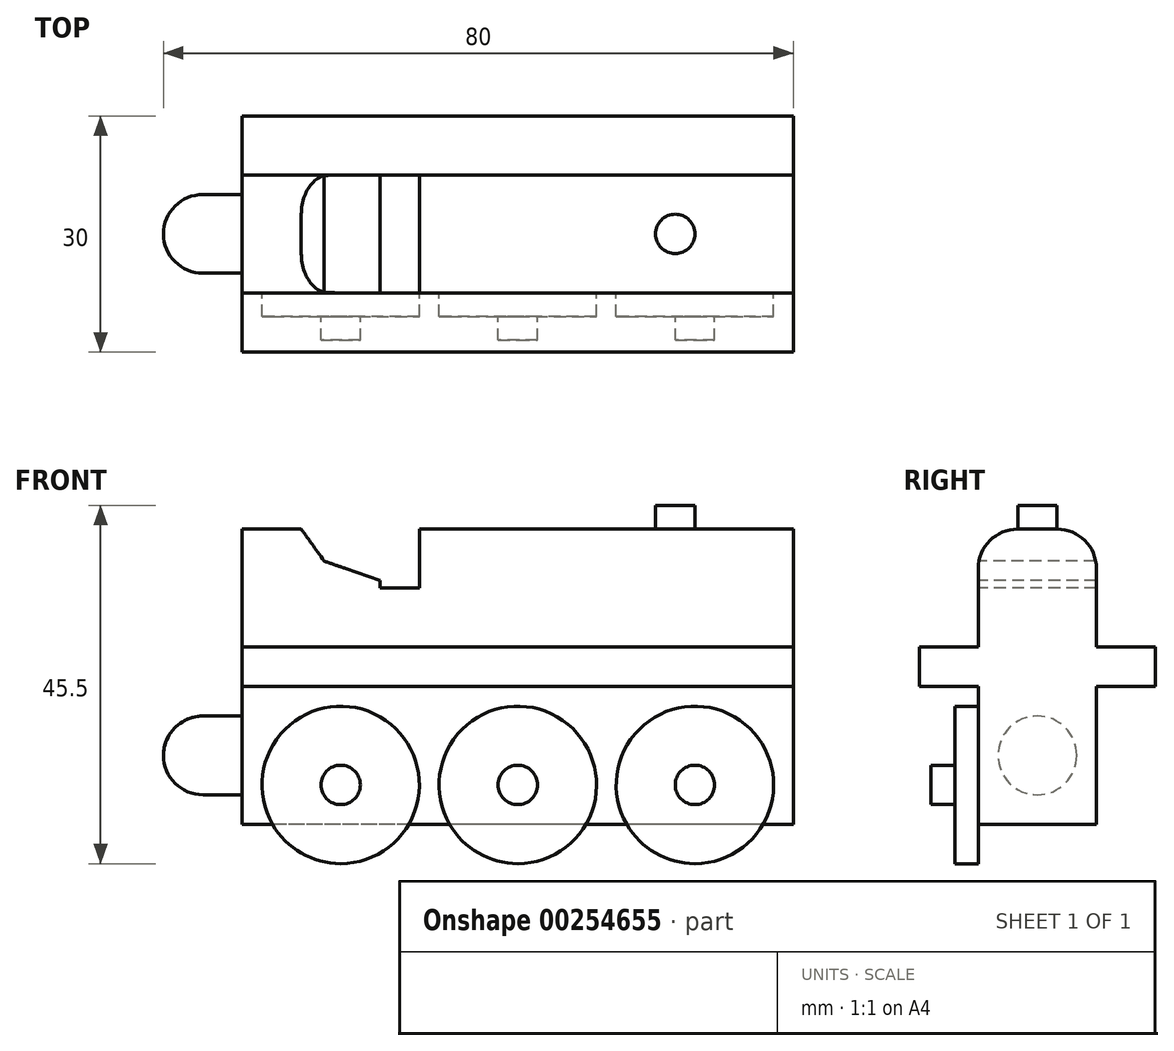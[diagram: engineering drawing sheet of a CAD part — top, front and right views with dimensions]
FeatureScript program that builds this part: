
annotation { "Feature Type Name" : "Feature", "Feature Type Description" : "" }
export const myFeature = defineFeature(function(context is Context, id is Id, definition is map)
    precondition{}
    {
        {
            var Q0;
            Q0=qCreatedBy(makeId("Top.planeOp"),FACE);
            var sketch = newSketch(context, id + "F0", { "sketchPlane" : qUnion([Q0])});
            skLineSegment(sketch, "E0.bottom", {"start": v(35, 7.5) * mm, "end": v(-35, 7.5) * mm});
            skLineSegment(sketch, "E0.top", {"start": v(35, -7.5) * mm, "end": v(-35, -7.5) * mm});
            skLineSegment(sketch, "E0.left", {"start": v(35, 7.5) * mm, "end": v(35, -7.5) * mm});
            skLineSegment(sketch, "E0.right", {"start": v(-35, 7.5) * mm, "end": v(-35, -7.5) * mm});
            skPoint(sketch, "E0.middle", {"position": v(0, 0) * mm});
            skSolve(sketch);
        }
        {
            var Q0;
            Q0 = qSketchRegion(id + "F0", true);
            extrude(context, id + "F1", {"entities" : qUnion([Q0]), "endBound" : BoundingType.SYMMETRIC, "depth" : 17.5 * mm});
        }
        {
            var Q0;
            Q0=makeQuery(id+"F1.opExtrude","CAP_FACE",FACE,{"disambiguationData":[OSD([sQuery(id+"F0.wireOp",EDGE,"E0.bottom"),sQuery(id+"F0.wireOp",EDGE,"E0.top"),sQuery(id+"F0.wireOp",EDGE,"E0.left"),sQuery(id+"F0.wireOp",EDGE,"E0.right")])],"isStart":false});
            var sketch = newSketch(context, id + "F2", { "sketchPlane" : qUnion([Q0])});
            skLineSegment(sketch, "E1.bottom", {"start": v(35, 15) * mm, "end": v(-35, 15) * mm});
            skLineSegment(sketch, "E1.top", {"start": v(35, -15) * mm, "end": v(-35, -15) * mm});
            skLineSegment(sketch, "E1.left", {"start": v(35, 15) * mm, "end": v(35, -15) * mm});
            skLineSegment(sketch, "E1.right", {"start": v(-35, 15) * mm, "end": v(-35, -15) * mm});
            skPoint(sketch, "E1.middle", {"position": v(0, 0) * mm});
            skSolve(sketch);
        }
        {
            var Q0;
            Q0 = qSketchRegion(id + "F2", true);
            extrude(context, id + "F3", {"entities" : qUnion([Q0]), "operationType" : NewBodyOperationType.ADD, "depth" : 5 * mm});
        }
        {
            var Q0;
            Q0=makeQuery(id+"F3.opExtrude","CAP_FACE",FACE,{"disambiguationData":[OSD([sQuery(id+"F2.wireOp",EDGE,"E1.bottom"),sQuery(id+"F2.wireOp",EDGE,"E1.top"),sQuery(id+"F2.wireOp",EDGE,"E1.left"),sQuery(id+"F2.wireOp",EDGE,"E1.right")])],"isStart":false});
            var sketch = newSketch(context, id + "F4", { "sketchPlane" : qUnion([Q0])});
            skLineSegment(sketch, "E2.bottom", {"start": v(35, 7.5) * mm, "end": v(-35, 7.5) * mm});
            skLineSegment(sketch, "E2.top", {"start": v(35, -7.5) * mm, "end": v(-35, -7.5) * mm});
            skLineSegment(sketch, "E2.left", {"start": v(35, 7.5) * mm, "end": v(35, -7.5) * mm});
            skLineSegment(sketch, "E2.right", {"start": v(-35, 7.5) * mm, "end": v(-35, -7.5) * mm});
            skPoint(sketch, "E2.middle", {"position": v(0, 0) * mm});
            skSolve(sketch);
        }
        {
            var Q0;
            Q0 = qSketchRegion(id + "F4", true);
            extrude(context, id + "F5", {"entities" : qUnion([Q0]), "operationType" : NewBodyOperationType.ADD, "depth" : 15 * mm});
        }
        {
            var Q0;
            Q0=qCreatedBy(makeId("Front.planeOp"),FACE);
            var sketch = newSketch(context, id + "F6", { "sketchPlane" : qUnion([Q0])});
            skLineSegment(sketch, "E3", {"start": v(-42.6, 0) * mm, "end": v(43.32, 0) * mm, "construction": true});
            skLineSegment(sketch, "E4.bottom", {"start": v(-35, 0) * mm, "end": v(-40, 0) * mm});
            skLineSegment(sketch, "E4.top", {"start": v(-35, -5) * mm, "end": v(-40, -5) * mm});
            skLineSegment(sketch, "E4.left", {"start": v(-35, 0) * mm, "end": v(-35, -5) * mm});
            skLineSegment(sketch, "E4.right", {"start": v(-40, 0) * mm, "end": v(-40, -5) * mm});
            skSolve(sketch);
        }
        {
            var Q0;
            Q0 = qSketchRegion(id + "F6", true);
            var Q1;
            Q1=sQuery(id+"F6.wireOp",EDGE,"E3");
            revolve(context, id + "F7", {"operationType" : NewBodyOperationType.ADD, "entities" : qUnion([Q0]), "axis" : qUnion([Q1]), "revolveType" : RevolveType.FULL});
        }
        {
            var Q0;
            Q0=makeQuery(id+"F1.opExtrude","SWEPT_FACE",FACE,{"disambiguationData":[OSD([sQuery(id+"F0.wireOp",EDGE,"E0.top")])]});
            var sketch = newSketch(context, id + "F8", { "sketchPlane" : qUnion([Q0])});
            skCircle(sketch, "E5", {"center": v(-22.5, -3.75) * mm, "radius": 10 * mm});
            skSolve(sketch);
        }
        {
            var Q0;
            Q0 = qSketchRegion(id + "F8", true);
            extrude(context, id + "F9", {"entities" : qUnion([Q0]), "operationType" : NewBodyOperationType.ADD, "depth" : 3 * mm});
        }
        {
            var Q0;
            Q0=makeQuery(id+"F1.opExtrude","SWEPT_FACE",FACE,{"disambiguationData":[OSD([sQuery(id+"F0.wireOp",EDGE,"E0.top")])]});
            var sketch = newSketch(context, id + "F10", { "sketchPlane" : qUnion([Q0])});
            skCircle(sketch, "E6", {"center": v(0, -3.75) * mm, "radius": 10 * mm});
            skSolve(sketch);
        }
        {
            var Q0;
            Q0 = qSketchRegion(id + "F10", true);
            extrude(context, id + "F11", {"entities" : qUnion([Q0]), "operationType" : NewBodyOperationType.ADD, "depth" : 3 * mm});
        }
        {
            var Q0;
            Q0=makeQuery(id+"F1.opExtrude","SWEPT_FACE",FACE,{"disambiguationData":[OSD([sQuery(id+"F0.wireOp",EDGE,"E0.top")])]});
            var sketch = newSketch(context, id + "F12", { "sketchPlane" : qUnion([Q0])});
            skCircle(sketch, "E7", {"center": v(22.5, -3.75) * mm, "radius": 10 * mm});
            skSolve(sketch);
        }
        {
            var Q0;
            Q0 = qSketchRegion(id + "F12", true);
            extrude(context, id + "F13", {"entities" : qUnion([Q0]), "operationType" : NewBodyOperationType.ADD, "depth" : 3 * mm});
        }
        {
            var Q0;
            Q0=makeQuery(id+"F9.opExtrude","CAP_FACE",FACE,{"disambiguationData":[OSD([sQuery(id+"F8.wireOp",EDGE,"E5")])],"isStart":false});
            var sketch = newSketch(context, id + "F14", { "sketchPlane" : qUnion([Q0])});
            skCircle(sketch, "E8", {"center": v(-22.5, -3.75) * mm, "radius": 2.5 * mm});
            skSolve(sketch);
        }
        {
            var Q0;
            Q0=makeQuery(id+"F14.imprint","IMPRINT",FACE,{"disambiguationData":[TD([[makeQuery(id+"F14.imprint","IMPRINT",EDGE,{"derivedFrom":sQuery(id+"F14.wireOp",EDGE,"E8")}),1.0]])]});
            extrude(context, id + "F15", {"entities" : qUnion([Q0]), "operationType" : NewBodyOperationType.ADD, "depth" : 3 * mm});
        }
        {
            var Q0;
            Q0=makeQuery(id+"F11.opExtrude","CAP_FACE",FACE,{"disambiguationData":[OSD([sQuery(id+"F10.wireOp",EDGE,"E6")])],"isStart":false});
            var sketch = newSketch(context, id + "F16", { "sketchPlane" : qUnion([Q0])});
            skCircle(sketch, "E9", {"center": v(0, -3.75) * mm, "radius": 2.5 * mm});
            skSolve(sketch);
        }
        {
            var Q0;
            Q0 = qSketchRegion(id + "F16", true);
            extrude(context, id + "F17", {"entities" : qUnion([Q0]), "operationType" : NewBodyOperationType.ADD, "depth" : 3 * mm});
        }
        {
            var Q0;
            Q0=makeQuery(id+"F13.opExtrude","CAP_FACE",FACE,{"disambiguationData":[OSD([sQuery(id+"F12.wireOp",EDGE,"E7")])],"isStart":false});
            var sketch = newSketch(context, id + "F18", { "sketchPlane" : qUnion([Q0])});
            skCircle(sketch, "E10", {"center": v(22.5, -3.75) * mm, "radius": 2.5 * mm});
            skSolve(sketch);
        }
        {
            var Q0;
            Q0 = qSketchRegion(id + "F18", true);
            extrude(context, id + "F19", {"entities" : qUnion([Q0]), "operationType" : NewBodyOperationType.ADD, "depth" : 3 * mm});
        }
        {
            var Q0;
            Q0=makeQuery(id+"F5.opExtrude","CAP_FACE",FACE,{"disambiguationData":[OSD([sQuery(id+"F4.wireOp",EDGE,"E2.bottom"),sQuery(id+"F4.wireOp",EDGE,"E2.top"),sQuery(id+"F4.wireOp",EDGE,"E2.left"),sQuery(id+"F4.wireOp",EDGE,"E2.right")])],"isStart":false});
            var sketch = newSketch(context, id + "F20", { "sketchPlane" : qUnion([Q0])});
            skCircle(sketch, "E11", {"center": v(20, 0) * mm, "radius": 2.5 * mm});
            skSolve(sketch);
        }
        {
            var Q0;
            Q0 = qSketchRegion(id + "F20", true);
            extrude(context, id + "F21", {"entities" : qUnion([Q0]), "operationType" : NewBodyOperationType.ADD, "depth" : 3 * mm});
        }
        {
            var Q0;
            Q0=makeQuery(id+"F5.opExtrude","SWEPT_FACE",FACE,{"disambiguationData":[OSD([sQuery(id+"F4.wireOp",EDGE,"E2.top")])]});
            var sketch = newSketch(context, id + "F22", { "sketchPlane" : qUnion([Q0])});
            skLineSegment(sketch, "E12", {"start": v(-27.5, 28.75) * mm, "end": v(-24.6, 24.68) * mm});
            skLineSegment(sketch, "E13", {"start": v(-24.6, 24.68) * mm, "end": v(-17.5, 22.25) * mm});
            skLineSegment(sketch, "E14", {"start": v(-17.5, 22.25) * mm, "end": v(-17.5, 21.25) * mm});
            skLineSegment(sketch, "E15", {"start": v(-17.5, 21.25) * mm, "end": v(-12.5, 21.25) * mm});
            skLineSegment(sketch, "E16", {"start": v(-12.5, 21.25) * mm, "end": v(-12.5, 28.75) * mm});
            skLineSegment(sketch, "E17", {"start": v(-12.5, 28.75) * mm, "end": v(-27.5, 28.75) * mm});
            skSolve(sketch);
        }
        {
            var Q0;
            Q0 = qSketchRegion(id + "F22", true);
            var Q1;
            Q1=makeQuery(id+"F5.opExtrude","SWEPT_FACE",FACE,{"disambiguationData":[OSD([sQuery(id+"F4.wireOp",EDGE,"E2.bottom")])]});
            extrude(context, id + "F23", {"entities" : qUnion([Q0]), "operationType" : NewBodyOperationType.REMOVE, "endBound" : BoundingType.UP_TO_SURFACE, "oppositeDirection" : true, "endBoundEntityFace" : qUnion([Q1]), "depth" : 25 * mm});
        }
        {
            var Q0;
            {var subQ0=sQuery(id+"F4.wireOp",EDGE,"E2.top");Q0=makeQuery(id+"F23.boolean.opBoolean","SPLIT",EDGE,{"disambiguationData":[TD([makeQuery(id+"F1.opExtrude","SWEPT_FACE",FACE,{"disambiguationData":[OSD([sQuery(id+"F0.wireOp",EDGE,"E0.left")])]})])],"derivedFrom":makeQuery(id+"F5.opExtrude","CAP_EDGE",EDGE,{"disambiguationData":[OSD([subQ0])],"isStart":false})});}
            var Q1;
            {var subQ1=sQuery(id+"F4.wireOp",EDGE,"E2.bottom");Q1=makeQuery(id+"F23.boolean.opBoolean","SPLIT",EDGE,{"disambiguationData":[TD([makeQuery(id+"F1.opExtrude","SWEPT_FACE",FACE,{"disambiguationData":[OSD([sQuery(id+"F0.wireOp",EDGE,"E0.left")])]})])],"derivedFrom":makeQuery(id+"F5.opExtrude","CAP_EDGE",EDGE,{"disambiguationData":[OSD([subQ1])],"isStart":false})});}
            fillet(context, id + "F24", {"entities" : qUnion([Q0, Q1]), "radius" : 5 * mm, "tangentPropagation" : true, "allowEdgeOverflow" : false});
        }
        {
            var Q0;
            {var subQ0=sQuery(id+"F4.wireOp",EDGE,"E2.top");Q0=makeQuery(id+"F23.boolean.opBoolean","SPLIT",EDGE,{"disambiguationData":[TD([makeQuery(id+"F1.opExtrude","SWEPT_FACE",FACE,{"disambiguationData":[OSD([sQuery(id+"F0.wireOp",EDGE,"E0.right")])]})])],"derivedFrom":makeQuery(id+"F5.opExtrude","CAP_EDGE",EDGE,{"disambiguationData":[OSD([subQ0])],"isStart":false})});}
            var Q1;
            {var subQ1=sQuery(id+"F4.wireOp",EDGE,"E2.bottom");Q1=makeQuery(id+"F23.boolean.opBoolean","SPLIT",EDGE,{"disambiguationData":[TD([makeQuery(id+"F1.opExtrude","SWEPT_FACE",FACE,{"disambiguationData":[OSD([sQuery(id+"F0.wireOp",EDGE,"E0.right")])]})])],"derivedFrom":makeQuery(id+"F5.opExtrude","CAP_EDGE",EDGE,{"disambiguationData":[OSD([subQ1])],"isStart":false})});}
            fillet(context, id + "F25", {"entities" : qUnion([Q0, Q1]), "radius" : 5 * mm, "tangentPropagation" : true, "allowEdgeOverflow" : false});
        }
        {
            var Q0;
            Q0=qCreatedBy(makeId("Front.planeOp"),FACE);
            var sketch = newSketch(context, id + "F26", { "sketchPlane" : qUnion([Q0])});
            skArc(sketch, "E18", {"start": v(-40, 5) * mm, "mid": v(-43.54, 3.54) * mm, "end": v(-45, 0) * mm});
            skLineSegment(sketch, "E19", {"start": v(-45, 0) * mm, "end": v(-40, 0) * mm});
            skLineSegment(sketch, "E20", {"start": v(-40, 5) * mm, "end": v(-40, 0) * mm});
            skLineSegment(sketch, "E21", {"start": v(-73.12, 0) * mm, "end": v(0, 0) * mm, "construction": true});
            skSolve(sketch);
        }
        {
            var Q0;
            Q0 = qSketchRegion(id + "F26", true);
            var Q1;
            Q1=sQuery(id+"F26.wireOp",EDGE,"E21");
            revolve(context, id + "F27", {"operationType" : NewBodyOperationType.ADD, "entities" : qUnion([Q0]), "axis" : qUnion([Q1]), "revolveType" : RevolveType.FULL});
        }
    });
